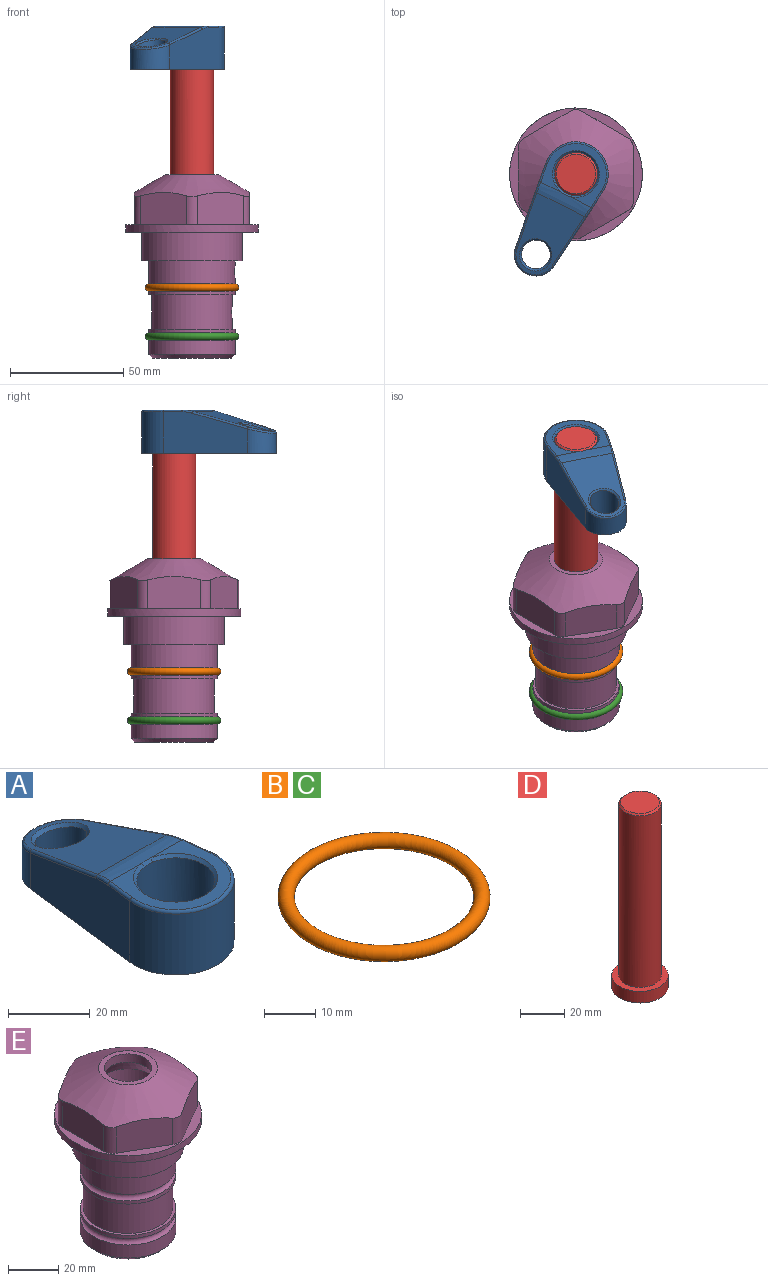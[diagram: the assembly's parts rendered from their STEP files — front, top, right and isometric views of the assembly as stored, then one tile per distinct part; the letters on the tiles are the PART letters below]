
ASSEMBLY  parts=5 mates=4
PART A: 31 faces, bbox 31.7x65.5x19.8 mm
  f0: plane 39.12x18.26mm, normal (0.99,0.12,0), area 612.2mm2, adj f1,f4,f7,f11,f13,f15
  f1: cylinder r=9.53mm len=18.91mm, axis (0,0,-1), area 296.1mm2, adj f0,f2,f7,f17
  f2: plane 39.12x18.26mm, normal (-0.99,0.12,0), area 612.2mm2, adj f1,f4,f7,f12,f14,f16
  f3: cylinder r=6.35mm len=12.7mm, axis (0,0,-1), area 362.4mm2, adj f7,f18
  f4: cylinder r=14.29mm len=28.58mm, axis (0,0,-1), area 882.2mm2, adj f0,f2,f7,f10
  f5: cylinder r=9.53mm len=19.05mm, axis (0,0,-1), area 1092.6mm2, adj f7,f19,f20
  f6: plane 26.99x23.69mm, normal (0,0,1), area 216.2mm2, adj f9,f10,f11,f12,f19
  f7: plane 63.5x28.58mm, normal (0,0,-1), area 661.8mm2, adj f0,f1,f2,f3,f4,f5,f22,f23
  f8: plane 33.52x23.6mm, normal (0,0.26,0.97), area 486mm2, adj f9,f15,f16,f17,f18
  f9: cylinder r=19.05mm len=24.72mm, axis (1,0,0), area 120.4mm2, adj f6,f8,f13,f14,f20
  f10: torus R=13.49mm, axis (0,0,1), area 59mm2, adj f4,f6,f11,f12
  f11: cylinder r=0.79mm len=8.67mm, axis (0.12,-0.99,0), area 10.8mm2, adj f0,f6,f10,f13
  f12: cylinder r=0.79mm len=8.67mm, axis (0.12,0.99,0), area 10.8mm2, adj f2,f6,f10,f14
  f13: bspline ~4.95x1.42mm, area 6.1mm2, adj f0,f9,f11,f15
  f14: bspline ~4.95x1.42mm, area 6.1mm2, adj f2,f9,f12,f16
  f15: cylinder r=0.79mm len=25.95mm, axis (0.12,-0.96,0.26), area 32.9mm2, adj f0,f8,f13,f17
  f16: cylinder r=0.79mm len=25.95mm, axis (0.12,0.96,-0.26), area 32.9mm2, adj f2,f8,f14,f17
  f17: bspline ~18.91x8.38mm, area 30mm2, adj f1,f8,f15,f16
  f18: bspline ~14.29x14.29mm, area 48.3mm2, adj f3,f8
  f19: cone r=9.53mm half-angle=45deg, axis (0,0,1), area 66.5mm2, adj f5,f6,f20
  f20: bspline ~3.22x0.96mm, area 3.5mm2, adj f5,f9,f19
  f21: plane 2.75x2.72mm, normal (0,0,-1), area 2.9mm2, adj f23,f25,f28
  f22: plane 23.05x15.88mm, normal (-0.99,-0.12,0), area 323.6mm2, adj f7,f25,f26,f27,f28,f29
  f23: plane 23.05x15.88mm, normal (0.99,-0.12,0), area 323.6mm2, adj f7,f21,f25,f27,f28,f30
  f24: cylinder r=9.53mm len=10.69mm, axis (0,0,-1), area 114.7mm2, adj f7,f27,f29,f30
  f25: cylinder r=12.7mm len=20.59mm, axis (0,0,-1), area 381.1mm2, adj f7,f21,f22,f23,f26,f28
  f26: plane 2.75x2.72mm, normal (0,0,-1), area 2.9mm2, adj f22,f25,f28
  f27: plane 19.72x18.37mm, normal (0,-0.26,-0.97), area 291.8mm2, adj f22,f23,f24,f28,f29,f30
  f28: cylinder r=15.88mm len=19.92mm, axis (1,0,0), area 54.8mm2, adj f21,f22,f23,f25,f26,f27
  f29: cylinder r=1.59mm len=11mm, axis (0,0,-1), area 34.7mm2, adj f7,f22,f24,f27
  f30: cylinder r=1.59mm len=11mm, axis (0,0,-1), area 34.7mm2, adj f7,f23,f24,f27
PART B: 1 faces, bbox 44.7x44.7x3.2 mm
  f0: torus R=19.05mm, axis (0,0,1), area 1193.9mm2
PART C: same geometry as B
PART D: 6 faces, bbox 25.4x25.4x101.6 mm
  f0: plane 17.46x17.46mm, normal (0,0,1), area 239.5mm2, adj f5
  f1: plane 25.4x25.4mm, normal (0,0,-1), area 506.7mm2, adj f2
  f2: cylinder r=12.7mm len=25.4mm, axis (0,0,1), area 506.7mm2, adj f1,f3
  f3: plane 25.4x25.4mm, normal (0,0,1), area 221.7mm2, adj f2,f4
  f4: cylinder r=9.53mm len=94.46mm, axis (0,0,1), area 5653mm2, adj f3,f5
  f5: cone r=8.73mm half-angle=45deg, axis (0,0,-1), area 64.4mm2, adj f0,f4
PART E: 36 faces, bbox 58.7x58.7x81 mm
  f0: cylinder r=17.78mm len=35.56mm, axis (0,0,1), area 1670.8mm2, adj f23,f24,f31
  f1: cylinder r=19.05mm len=38.1mm, axis (0,0,1), area 1191.9mm2, adj f26,f27,f30
  f2: plane 58.66x58.66mm, normal (0,0,-1), area 1150.6mm2, adj f3,f28
  f3: cylinder r=29.33mm len=58.66mm, axis (0,0,-1), area 585.1mm2, adj f2,f4
  f4: plane 58.66x58.66mm, normal (0,0,1), area 475.9mm2, adj f3,f5,f6,f7,f8,f9,f10,f11
  f5: plane 20.32x14.34mm, normal (-0.5,0.87,0), area 324.4mm2, adj f4,f15,f16,f17
  f6: plane 20.32x14.34mm, normal (0.5,0.87,0), area 324.4mm2, adj f4,f14,f15,f17
  f7: plane 23.48x14.34mm, normal (1,0,0), area 324.4mm2, adj f4,f13,f14,f17
  f8: plane 20.32x14.34mm, normal (0.5,-0.87,0), area 324.4mm2, adj f4,f12,f13,f17
  f9: plane 20.32x14.34mm, normal (-0.5,-0.87,0), area 324.4mm2, adj f4,f11,f12,f17
  f10: plane 23.48x14.34mm, normal (-1,0,0), area 324.4mm2, adj f4,f11,f16,f17
  f11: cylinder r=5.08mm len=12.85mm, axis (0,0,-1), area 67.2mm2, adj f4,f9,f10,f17
  f12: cylinder r=5.08mm len=12.85mm, axis (0,0,-1), area 67.2mm2, adj f4,f8,f9,f17
  f13: cylinder r=5.08mm len=12.85mm, axis (0,0,-1), area 67.2mm2, adj f4,f7,f8,f17
  f14: cylinder r=5.08mm len=12.85mm, axis (0,0,-1), area 67.2mm2, adj f4,f6,f7,f17
  f15: cylinder r=5.08mm len=12.85mm, axis (0,0,-1), area 67.2mm2, adj f4,f5,f6,f17
  f16: cylinder r=5.08mm len=12.85mm, axis (0,0,-1), area 67.2mm2, adj f4,f5,f10,f17
  f17: cone r=11.73mm half-angle=60deg, axis (0,0,-1), area 2071.8mm2, adj f5,f6,f7,f8,f9,f10,f11,f12
  f18: plane 23.46x23.46mm, normal (0,0,1), area 147.4mm2, adj f17,f35
  f19: plane 34.93x34.93mm, normal (0,0,-1), area 958mm2, adj f29
  f20: cylinder r=19.05mm len=38.1mm, axis (0,0,1), area 760.1mm2, adj f21,f29
  f21: torus R=19.05mm, axis (0,0,1), area 565.3mm2, adj f20,f22
  f22: cylinder r=19.05mm len=38.1mm, axis (0,0,1), area 190mm2, adj f21,f23
  f23: plane 38.1x38.1mm, normal (0,0,1), area 146.9mm2, adj f0,f22
  f24: plane 38.1x38.1mm, normal (0,0,-1), area 146.9mm2, adj f0,f25
  f25: cylinder r=19.05mm len=38.1mm, axis (0,0,1), area 190mm2, adj f24,f26
  f26: torus R=19.05mm, axis (0,0,1), area 565.3mm2, adj f1,f25
  f27: plane 44.45x44.45mm, normal (0,0,-1), area 411.7mm2, adj f1,f28
  f28: cylinder r=22.23mm len=44.45mm, axis (0,0,1), area 1773.5mm2, adj f2,f27
  f29: cone r=19.05mm half-angle=45deg, axis (0,0,1), area 257.5mm2, adj f19,f20
  f30: cylinder r=3.17mm len=6.75mm, axis (-1,0,0), area 128mm2, adj f1,f33
  f31: cylinder r=3.17mm len=6.35mm, axis (-1,0,0), area 102.5mm2, adj f0,f33
  f32: plane 25.4x25.4mm, normal (0,0,1), area 506.7mm2, adj f33
  f33: cylinder r=12.7mm len=66.42mm, axis (0,0,-1), area 5236.2mm2, adj f30,f31,f32,f34
  f34: cone r=9.53mm half-angle=30deg, axis (0,0,-1), area 443.4mm2, adj f33,f35
  f35: cylinder r=9.53mm len=19.05mm, axis (0,0,-1), area 240.9mm2, adj f18,f34
PLACE A rot(axis=(0,0,1),153.5deg) t=(0,0,27.55)mm
PLACE B at identity
PLACE C t=(0,0,-21.59)mm
PLACE D rot(axis=(0,0,1),153.5deg) t=(0,0,27.55)mm
PLACE E at identity fixed
MATE fastened A.f4 <-> D.f2  axis (0,0,1) through (0,0,91.05)mm
MATE cylindrical E.f0 <-> D.f2  axis (0,0,1) through (0,0,-50.55)mm
MATE fastened E.f0 <-> C.f0  axis (0,0,1) through (0,0,-46.1)mm
MATE fastened E.f0 <-> B.f0  axis (0,0,1) through (0,0,-24.51)mm
